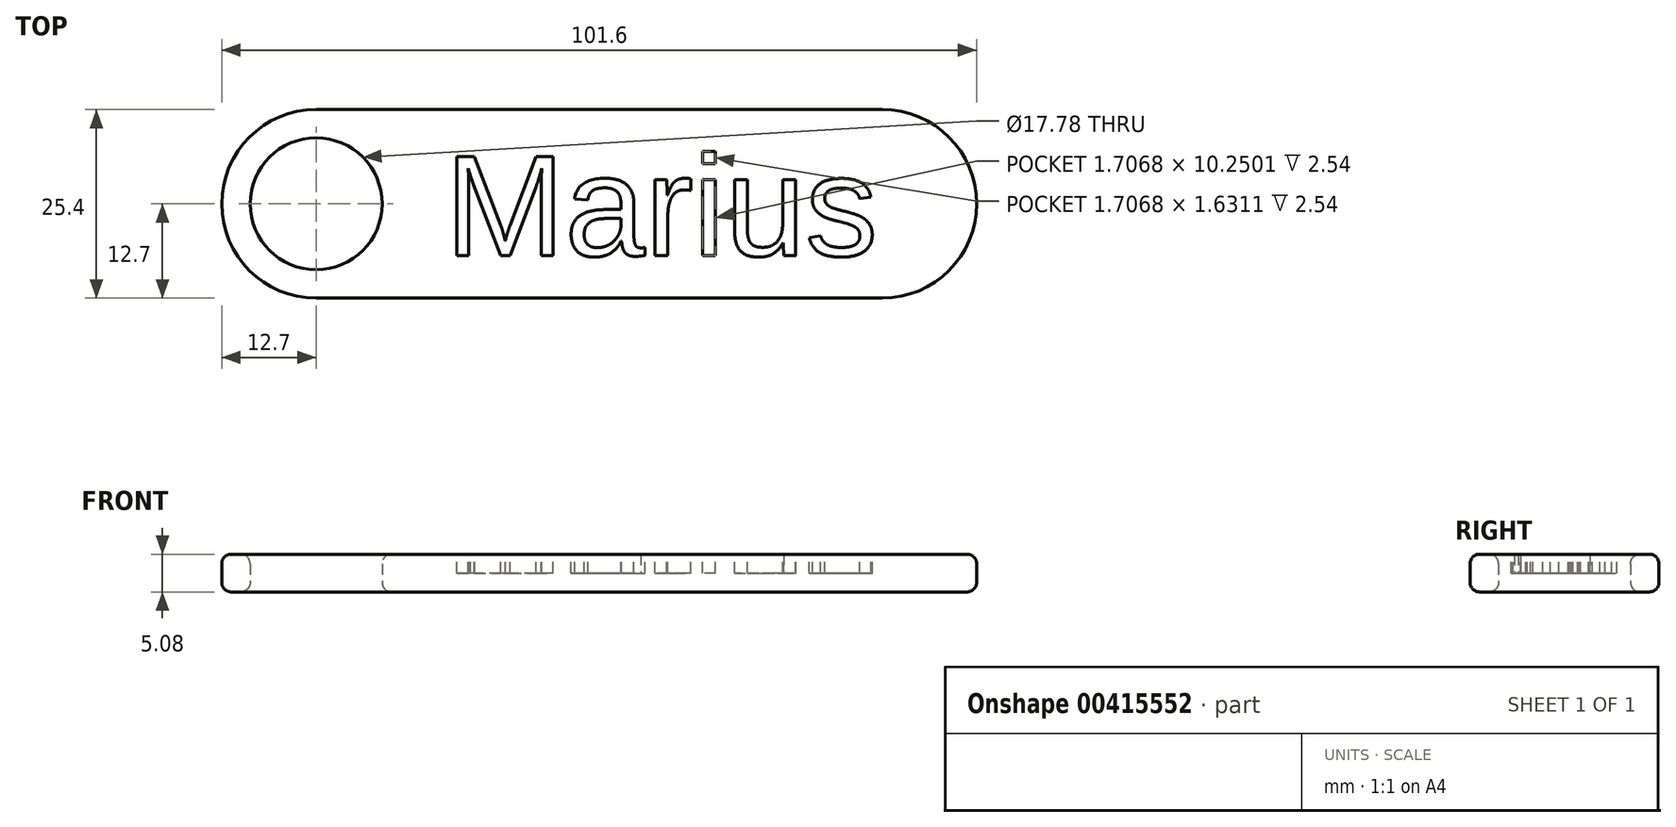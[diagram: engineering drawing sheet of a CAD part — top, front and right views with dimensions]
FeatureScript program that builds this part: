
annotation { "Feature Type Name" : "Feature", "Feature Type Description" : "" }
export const myFeature = defineFeature(function(context is Context, id is Id, definition is map)
    precondition{}
    {
        {
            var Q0;
            Q0=qCreatedBy(makeId("Top.planeOp"),FACE);
            var sketch = newSketch(context, id + "F0", { "sketchPlane" : qUnion([Q0])});
            skLineSegment(sketch, "E0.bottom", {"start": v(38.1, -12.7) * mm, "end": v(-38.1, -12.7) * mm});
            skLineSegment(sketch, "E0.top", {"start": v(38.1, 12.7) * mm, "end": v(-38.1, 12.7) * mm});
            skPoint(sketch, "E0.middle", {"position": v(0, 0) * mm});
            skArc(sketch, "E1", {"start": v(38.1, -12.7) * mm, "mid": v(50.8, 0) * mm, "end": v(38.1, 12.7) * mm});
            skArc(sketch, "E2", {"start": v(-38.1, 12.7) * mm, "mid": v(-50.8, 0) * mm, "end": v(-38.1, -12.7) * mm});
            skCircle(sketch, "E3", {"center": v(-38.1, 0) * mm, "radius": 8.9 * mm});
            skSolve(sketch);
        }
        {
            var Q0;
            Q0=makeQuery(id+"F0.imprint","IMPRINT",FACE,{"disambiguationData":[TD([[makeQuery(id+"F0.imprint","IMPRINT",EDGE,{"derivedFrom":sQuery(id+"F0.wireOp",EDGE,"E0.bottom")}),-1.0]])]});
            extrude(context, id + "F1", {"entities" : qUnion([Q0]), "depth" : 5.08 * mm});
        }
        {
            var Q0;
            Q0=makeQuery(id+"F1.opExtrude","CAP_FACE",FACE,{"disambiguationData":[OSD([sQuery(id+"F0.wireOp",EDGE,"E0.bottom"),sQuery(id+"F0.wireOp",EDGE,"E0.top"),sQuery(id+"F0.wireOp",EDGE,"E1"),sQuery(id+"F0.wireOp",EDGE,"E2"),sQuery(id+"F0.wireOp",EDGE,"E3")])],"isStart":false});
            var sketch = newSketch(context, id + "F2", { "sketchPlane" : qUnion([Q0])});
            skText(sketch, "E4", { "text": "Marius", "fontName": "Arimo-Regular.ttf"});
            const initialGuessF2  = {"E4": [-0.02076, -0.00699, 1, 0, 0.01397]};
            skSetInitialGuess(sketch, initialGuessF2);
            skSolve(sketch);
        }
        {
            var Q0;
            Q0=qSketchRegion(id+"F2",true);
            extrude(context, id + "F3", {"entities" : qUnion([Q0]), "operationType" : NewBodyOperationType.REMOVE, "oppositeDirection" : true, "depth" : 2.54 * mm});
        }
        {
            var Q0;
            Q0=makeQuery(id+"F1.opExtrude","CAP_EDGE",EDGE,{"disambiguationData":[OSD([sQuery(id+"F0.wireOp",EDGE,"E2")])],"isStart":false});
            var Q1;
            Q1=makeQuery(id+"F1.opExtrude","CAP_FACE",FACE,{"disambiguationData":[OSD([sQuery(id+"F0.wireOp",EDGE,"E0.bottom"),sQuery(id+"F0.wireOp",EDGE,"E0.top"),sQuery(id+"F0.wireOp",EDGE,"E1"),sQuery(id+"F0.wireOp",EDGE,"E2"),sQuery(id+"F0.wireOp",EDGE,"E3")])],"isStart":true});
            var Q2;
            Q2=makeQuery(id+"F1.opExtrude","CAP_EDGE",EDGE,{"disambiguationData":[OSD([sQuery(id+"F0.wireOp",EDGE,"E3")])],"isStart":false});
            fillet(context, id + "F4", {"entities" : qUnion([Q0, Q1, Q2]), "radius" : 1.27 * mm, "tangentPropagation" : true, "allowEdgeOverflow" : false});
        }
    });
